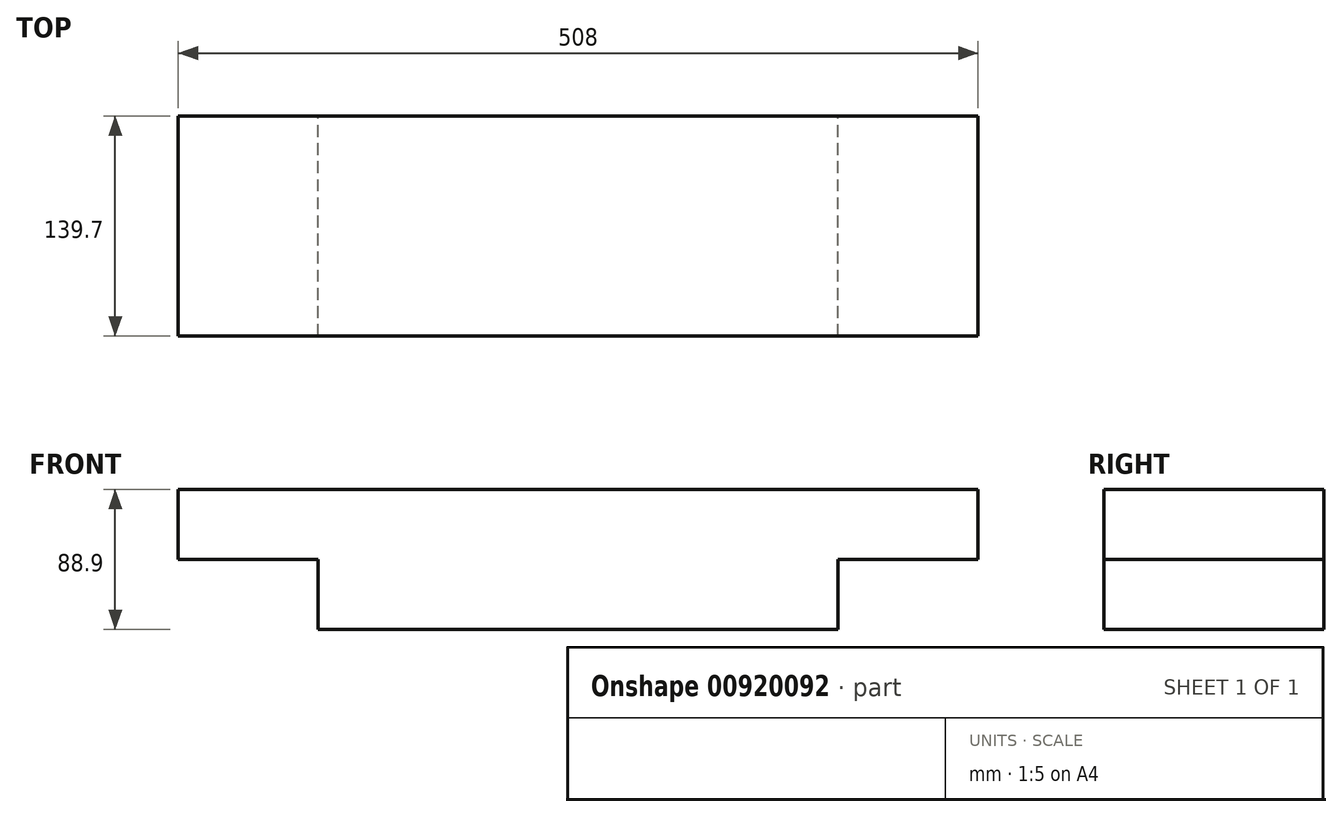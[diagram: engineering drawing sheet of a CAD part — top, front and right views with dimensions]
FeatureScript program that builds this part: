
annotation { "Feature Type Name" : "Feature", "Feature Type Description" : "" }
export const myFeature = defineFeature(function(context is Context, id is Id, definition is map)
    precondition{}
    {
        {
            var Q0;
            Q0=qCreatedBy(makeId("Top.planeOp"),FACE);
            var sketch = newSketch(context, id + "F0", { "sketchPlane" : qUnion([Q0])});
            skLineSegment(sketch, "E0.bottom", {"start": v(0, 0) * mm, "end": v(508, 0) * mm});
            skLineSegment(sketch, "E0.top", {"start": v(0, 139.7) * mm, "end": v(508, 139.7) * mm});
            skLineSegment(sketch, "E0.left", {"start": v(0, 0) * mm, "end": v(0, 139.7) * mm});
            skLineSegment(sketch, "E0.right", {"start": v(508, 0) * mm, "end": v(508, 139.7) * mm});
            skSolve(sketch);
        }
        {
            var Q0;
            Q0=makeQuery(id+"F0.imprint","IMPRINT",FACE,{"disambiguationData":[TD([[makeQuery(id+"F0.imprint","IMPRINT",EDGE,{"derivedFrom":sQuery(id+"F0.wireOp",EDGE,"E0.bottom")}),1.0]])]});
            extrude(context, id + "F1", {"entities" : qUnion([Q0]), "depth" : 88.9 * mm, "offsetDistance" : 25.4 * mm});
        }
        {
            var Q0;
            Q0=makeQuery(id+"F1.opExtrude","CAP_FACE",FACE,{"disambiguationData":[OSD([sQuery(id+"F0.wireOp",EDGE,"E0.bottom"),sQuery(id+"F0.wireOp",EDGE,"E0.top"),sQuery(id+"F0.wireOp",EDGE,"E0.left"),sQuery(id+"F0.wireOp",EDGE,"E0.right")])],"isStart":true});
            var sketch = newSketch(context, id + "F2", { "sketchPlane" : qUnion([Q0])});
            skLineSegment(sketch, "E1.bottom", {"start": v(0, 0) * mm, "end": v(88.9, 0) * mm});
            skLineSegment(sketch, "E1.top", {"start": v(0, -139.7) * mm, "end": v(88.9, -139.7) * mm});
            skLineSegment(sketch, "E1.left", {"start": v(0, 0) * mm, "end": v(0, -139.7) * mm});
            skLineSegment(sketch, "E1.right", {"start": v(88.9, 0) * mm, "end": v(88.9, -139.7) * mm});
            skLineSegment(sketch, "E2.bottom", {"start": v(508, 0) * mm, "end": v(419.1, 0) * mm});
            skLineSegment(sketch, "E2.top", {"start": v(508, -139.7) * mm, "end": v(419.1, -139.7) * mm});
            skLineSegment(sketch, "E2.left", {"start": v(508, 0) * mm, "end": v(508, -139.7) * mm});
            skLineSegment(sketch, "E2.right", {"start": v(419.1, 0) * mm, "end": v(419.1, -139.7) * mm});
            skSolve(sketch);
        }
        {
            var Q0;
            Q0 = qSketchRegion(id + "F2", true);
            extrude(context, id + "F3", {"entities" : qUnion([Q0]), "operationType" : NewBodyOperationType.REMOVE, "oppositeDirection" : true, "depth" : 44.45 * mm, "offsetDistance" : 25.4 * mm});
        }
    });
